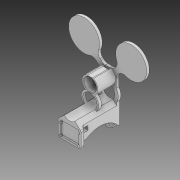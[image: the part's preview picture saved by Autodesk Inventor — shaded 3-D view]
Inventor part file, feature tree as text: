
AUTODESK INVENTOR PART (.ipt)
format: ipt  version: 2020 (Build 240168000, 168)  size: 454,656 bytes
history: native  units: mm
features: extrude x14, sketch x14, fillet x3, chamfer x3, mirror x1
ambient origin geometry x8: Origin, YZ Plane, XZ Plane, XY Plane, X Axis, Y Axis, Z Axis, Center Point
bodies: Solid1 (feature_tree)
feature tree (35):
  extrude  "Extrusion1"  Depth=20.6375mm
  extrude  "Extrusion2"  Depth=3.96875mm
  extrude  "Extrusion3"  Depth=19.05mm
  extrude  "Extrusion4"  Depth=5.5mm
  extrude  "Extrusion5"  Depth=3.0mm
  extrude  "Extrusion7"  Depth=9.0mm
  extrude  "Extrusion8"  TaperAngle=45.0deg  [1 undecoded]
  mirror  "Mirror2"
  fillet  "Fillet2"  Radius=2.0mm
  extrude  "Extrusion9"  Depth=1.0mm
  chamfer  "Chamfer1"  Distance=7.75mm
  extrude  "Extrusion10"  Depth=3.0mm
  extrude  "Extrusion11"  Depth=40.0mm
  extrude  "Extrusion12"  Depth=3.0mm TaperAngle=0.0deg
  fillet  "Fillet3"  Radius=2.5mm
  extrude  "Extrusion13"  Depth=2.0mm TaperAngle=0.0deg
  fillet  "Fillet4"  Radius=2.5mm
  extrude  "Extrusion14"  Depth=10.0mm TaperAngle=0.0deg
  chamfer  "Chamfer2"  Distance=4.2mm
  extrude  "Extrusion15"  Depth=3.0mm TaperAngle=0.0deg
  chamfer  "Chamfer3"  Distance=10.0mm
  sketch  "Sketch1"  dims[d0=20.6375mm d1=23.8125mm d2=32.816122mm]
  sketch  "Sketch2"  dims[d3=23.8125mm d4=3.96875mm]
  sketch  "Sketch3"  dims[d5=19.05mm d6=9.797mm]
  sketch  "Sketch4"  dims[d7=5.5mm d8=16.1mm]
  sketch  "Sketch5"  dims[d9=3.0mm d10=0.0mm d11=14.1mm]
  sketch  "Sketch7"  dims[d12=18.0mm d13=8.0mm d14=9.0mm]
  sketch  "Sketch8"  dims[d15=20.0mm d16=0.0mm d17=45.0deg d18=2.0mm]
  sketch  "Sketch9"  dims[d19=0.0mm d20=0.0mm d21=1.0mm]
  sketch  "Sketch10"  dims[d22=1.0mm]
  sketch  "Sketch11"  dims[d23=2.5mm d24=7.75mm d25=0.0mm]
  sketch  "Sketch12"  dims[d26=9.5mm d27=3.0mm]
  sketch  "Sketch13"  dims[d28=40.0mm d29=0.0mm d33=18.0mm]
  sketch  "Sketch14"  dims[d34=26.0mm d35=3.0mm d36=0.0mm]
  sketch  "Sketch15"  dims[d37=2.4mm d38=12.5mm d39=20.5mm d40=2.5mm d41=2.0mm d42=0.0mm d43=2.5mm d44=10.0mm d45=0.0mm d46=4.2mm d47=7.75mm d48=0.0mm d49=10.0mm d50=0.0mm d51=3.0mm d52=1.5mm d53=0.0mm d54=2.5mm d55=12.0mm d56=2.0mm d57=45.0deg d58=27.0mm d59=35.0mm d60=1.5mm d61=0.0mm d62=7.0mm d63=0.5mm d64=2.0mm d65=45.0deg d66=2.0mm d67=3.0mm d68=0.0mm d69=11.90625mm d70=45.0deg d71=45.0deg d72=26.876241mm d73=5.0mm d74=3.5mm d75=2.5mm d76=2.0mm d77=0.0mm d78=1.0mm d79=3.0mm d80=45.0deg]
note: 1 required parameter value undecoded (feature->parameter linkage not recoverable at this tier; creation-order binding heuristic only, values carry confidence <= 0.55)
